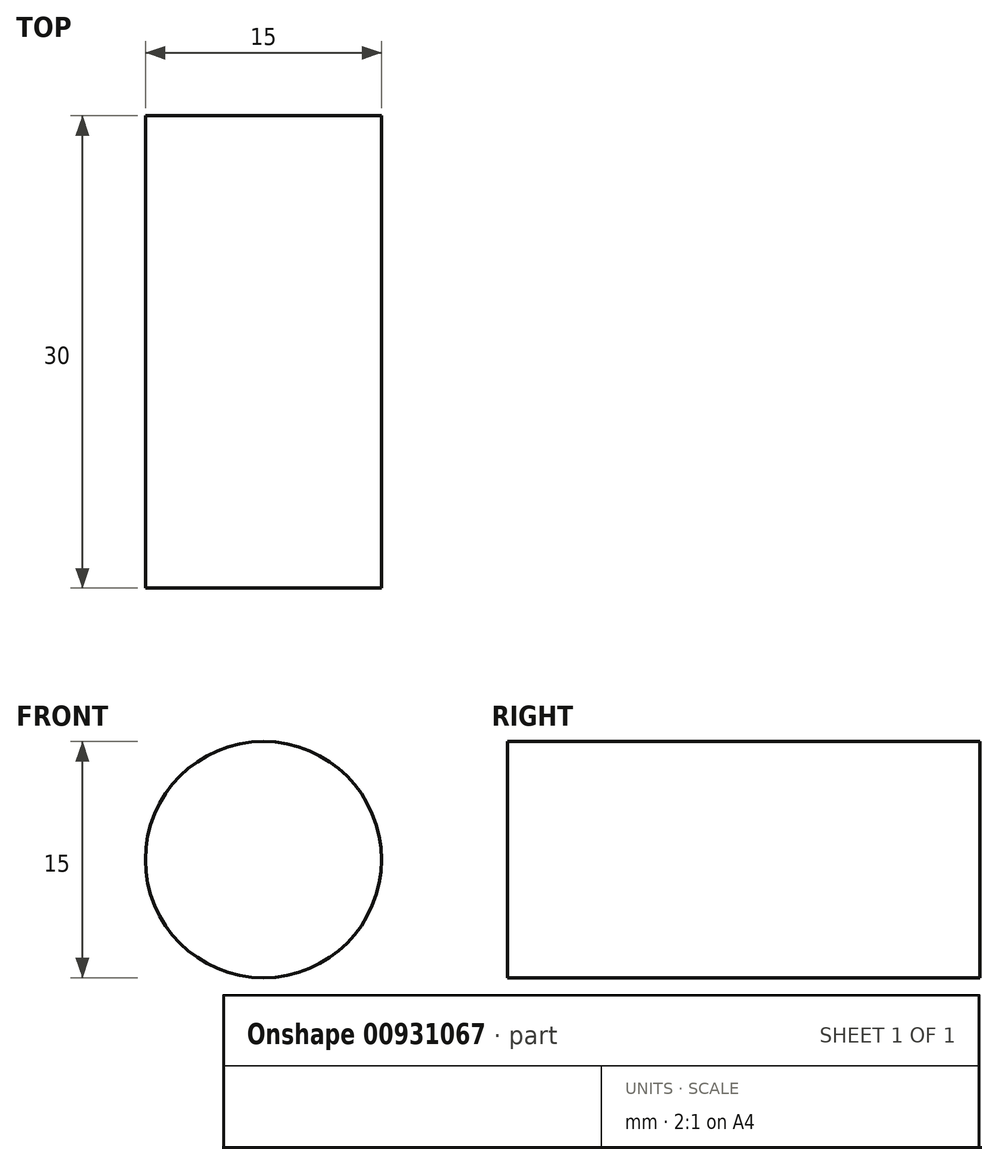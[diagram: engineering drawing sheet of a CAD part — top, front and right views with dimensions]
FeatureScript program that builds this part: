
annotation { "Feature Type Name" : "Feature", "Feature Type Description" : "" }
export const myFeature = defineFeature(function(context is Context, id is Id, definition is map)
    precondition{}
    {
        {
            var Q0;
            Q0=qCreatedBy(makeId("Front.planeOp"),FACE);
            var sketch = newSketch(context, id + "F0", { "sketchPlane" : qUnion([Q0])});
            skCircle(sketch, "E0", {"center": v(0, 0) * mm, "radius": 7.5 * mm});
            skSolve(sketch);
        }
        {
            var Q0;
            Q0=makeQuery(id+"F0.imprint","IMPRINT",FACE,{"disambiguationData":[TD([[makeQuery(id+"F0.imprint","IMPRINT",EDGE,{"derivedFrom":sQuery(id+"F0.wireOp",EDGE,"E0")}),1.0]])]});
            extrude(context, id + "F1", {"entities" : qUnion([Q0]), "depth" : 30 * mm, "offsetDistance" : 25 * mm});
        }
    });
